# Revit family: Electronics_Compact-Audio-DSP_Biamp_TesiraFORTE-X_Meeting-Room-DSP___
name_source: partatom
category: Communication Devices
units: mm (PartAtom-declared; Revit-internal decimal feet)

## family parameters
Cut with Voids When Loaded = Yes
Host = Face
Maintain Annotation Orientation = No
OmniClass Number = 23.85.10.14
OmniClass Title = Visual Information Systems
Part Type = Normal
Room Calculation Point = No
Round Connector Dimension = Use Diameter
Shared = No

## types (3) — shared parameters
A/D - D/A Converters = 24-bit
Altitude = 0-6,600 ft (0-2000m) MSL
Apparent Load = 150 VA
Bit Depth = 16-bit / 24-bit
Compliance = FCC Part 15B (USA), Canada ICES-003 (A) / NMB-003 (A), CE marked (Europe), UL und C-UL listed (USA and Canada), RCM (Australia), RoHS Directive (Europe)
Connector Description = 100 - 240V 50/60Hz
Cross Talk = 0dB Gain, +4dBu In: < -85dB channel to channel at 1kHz; 54dB Gain, -50dBu In: < -75dB channel to channel at 1kHz;
Default Elevation = 48 "
Depth = 8.102 "
Dynamic Range = 22Hz to 22kHz, 0dB gain: > 108dB
EIN = < -125dBu
Frequency Response = 20Hz to 20kHz, +4dBu output: +0.25 dB/-0.5 dB
Height = 1.5 "
Housing Material = Biamp - Metal - Dark Gray
Humidity = 0-98% relative humidity (non-condensing)
Input Gain Range = 0-66dB
Input Impedance = 8 kohm
Manufacturer = Biamp
Max Power Consumption = 150 W
Maximum AVB Stream Passthrough = 150
Maximum Input = +24dBu
Maximum Number of AVB Channels = 128x128
Maximum Number of AVB Streams = 64x64
Maximum Number of Dante Channels = 32x32
Maximum Number of Dante Flows = 32x32
Maximum Output = +24dBu, +18dBu, +12dBu
No Mount = No mount
Number of Channels = up to 2x2
Number of Poles = 1
Output Impedance = 207 ohm
Phantom Power = +48VDC (7mA/input)
Power Factor = 1
Product Documentation Link = https://downloads.biamp.com
Product Page URL = https://www.biamp.com
Product data url = https://www.bimobject.com
Sample Rate = 48kHz
Sampling Rate = 48kHz
THD+N = 0dB Gain, +4dBu In: < 0.006% at 22Hz~22kHz; 54dB Gain, -50dBu In: < 0.040% at 22Hz~22kHz;
Temperature Range = 32 - 104° F (0 - 40° C)
URL = https://www.biamp.com
Voltage = 120 V
Weight = 1.90 lbf
Width = 8.102 "
_Plenum Box 12x12 = Plenum Box 12x12
_RMX 100 Rack Shelf = RMX 100 Rack Shelf

## per-type parameters (varying)
| type | Description | Model |
| X 400 | TesiraFORTÉ® X 400 Meeting Room DSP | TesiraFORTÉ X 400 |
| X 800 | TesiraFORTÉ® X 800 Meeting Room DSP | TesiraFORTÉ X 800 |
| X 1600 | TesiraFORTÉ® X 1600 Meeting Room DSP | TesiraFORTÉ X 1600 |

## geometry (parser evidence)
native form markers: Sweep x11
no freeform markers — native parametric forms only
